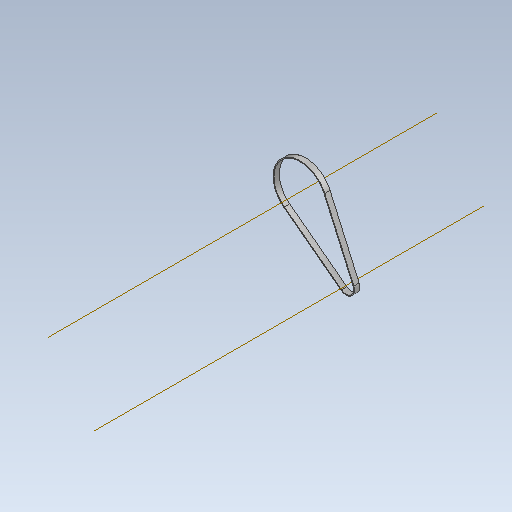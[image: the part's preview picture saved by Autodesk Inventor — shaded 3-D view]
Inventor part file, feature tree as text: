
AUTODESK INVENTOR PART (.ipt)
format: ipt  version: 2020 (Build 240168000, 168)  size: 100,864 bytes
history: native  units: mm (DEFAULTED — no unit token found)
features: other x4, plane x2, sketch x1, sweep x1
ambient origin geometry x8: Origin, YZ Plane, XZ Plane, XY Plane, X Axis, Y Axis, Z Axis, Center Point
bodies: Solid1 (feature_tree)
feature tree (8):
  sketch  "Sketch Path"  dims[d0=4.0mm d2=0.0mm d4=0.3mm d5=0.3mm d6=0.0mm d7=0.0mm d8=0.0mm d9=0.0mm d10=0.0mm d11=0.0mm]
  other  "Cross Section Plane"
  other  "Work Axis1"
  other  "Work Axis2"
  plane  "Work Plane2"
  plane  "Work Plane3"
  sweep  "Belt"
  other  "Cross Section"
